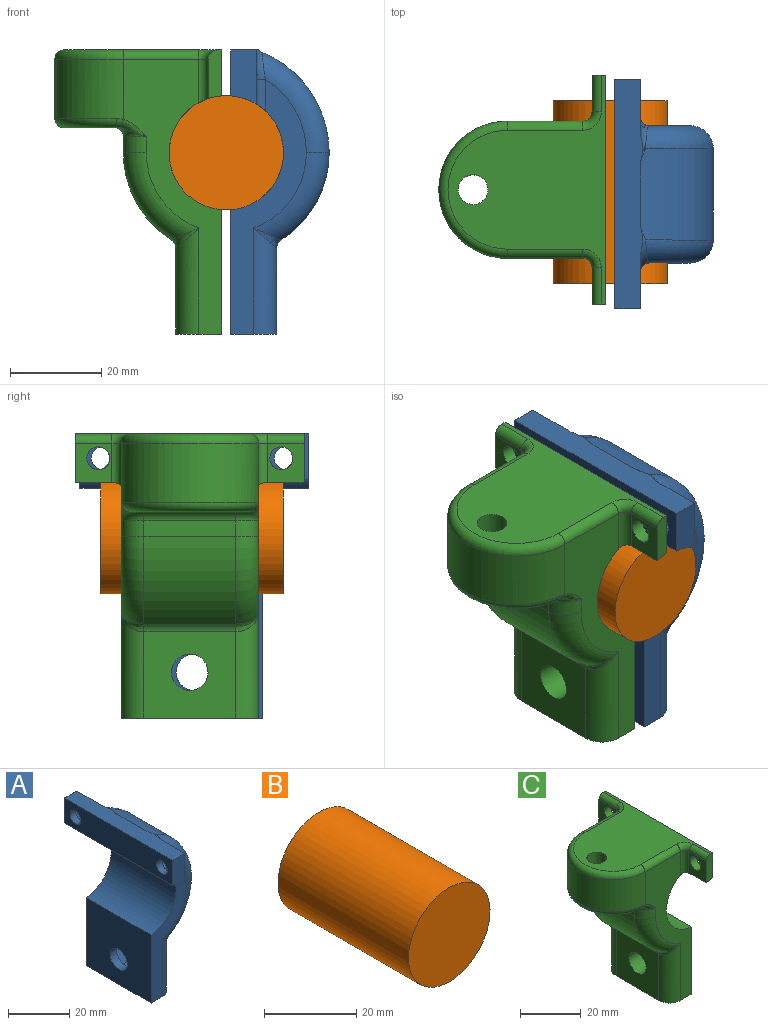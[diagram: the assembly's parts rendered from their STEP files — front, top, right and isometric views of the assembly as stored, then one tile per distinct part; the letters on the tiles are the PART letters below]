
ASSEMBLY  parts=3 mates=2
PART A: 51 faces, bbox 23.8x50.3x63.8 mm
  f0: cylinder r=2.5mm len=5mm, axis (-1,0,0), area 40mm2, adj f8,f37
  f1: cylinder r=2.5mm len=5mm, axis (-1,0,0), area 40mm2, adj f8,f30
  f2: cylinder r=4mm len=8mm, axis (-1,0,0), area 75.4mm2, adj f10,f13
  f3: plane 30x10mm, normal (0,0,-1), area 289.3mm2, adj f4,f10,f11,f12,f39,f42
  f4: plane 20x18.86mm, normal (1,0,0), area 230.9mm2, adj f3,f14,f15,f16,f17,f18,f19,f39
  f5: cylinder r=22.5mm len=20mm, axis (0,1,0), area 455.2mm2, adj f6,f40,f43,f45
  f6: cylinder r=23.81mm len=22.48mm, axis (0,1,0), area 582.6mm2, adj f5,f7,f38,f41,f48,f50
  f7: plane 50.33x6.43mm, normal (0,0,1), area 281.6mm2, adj f6,f8,f20,f21,f22,f23,f48,f50
  f8: plane 50x10.02mm, normal (-1,0,0), area 461.6mm2, adj f0,f1,f7,f9,f20,f23
  f9: cylinder r=12.5mm len=50mm, axis (0,1,0), area 1240.8mm2, adj f8,f10,f11,f12,f20,f21,f22,f23
  f10: plane 30x27.17mm, normal (-1,0,0), area 764.8mm2, adj f2,f3,f9,f11,f12
  f11: plane 55.65x16.5mm, normal (0,-1,0), area 302mm2, adj f3,f9,f10,f41,f42,f43,f47
  f12: plane 55.65x16.5mm, normal (0,1,0), area 302mm2, adj f3,f9,f10,f38,f39,f40,f49
  f13: plane 15.01x13mm, normal (1,0,0), area 96.1mm2, adj f2,f14,f15,f16,f17,f18,f19
  f14: plane 7.51x7mm, normal (0,0,1), area 52.5mm2, adj f4,f13,f15,f19
  f15: plane 7x6.5mm, normal (0,-0.87,0.5), area 52.5mm2, adj f4,f13,f14,f16
  f16: plane 7x6.5mm, normal (0,-0.87,-0.5), area 52.5mm2, adj f4,f13,f15,f17
  f17: plane 7.51x7mm, normal (0,0,-1), area 52.5mm2, adj f4,f13,f16,f18
  f18: plane 7x6.5mm, normal (0,0.87,-0.5), area 52.5mm2, adj f4,f13,f17,f19
  f19: plane 7x6.5mm, normal (0,0.87,0.5), area 52.5mm2, adj f4,f13,f14,f18
  f20: plane 11.83x5.55mm, normal (0,1,0), area 59.2mm2, adj f7,f8,f9,f21
  f21: plane 11.83x10.98mm, normal (1,0,0), area 59.4mm2, adj f7,f9,f20,f24,f25,f26,f27,f28
  f22: plane 11.83x10.98mm, normal (1,0,0), area 59.4mm2, adj f7,f9,f23,f31,f32,f33,f34,f35
  f23: plane 11.83x5.55mm, normal (0,-1,0), area 59.2mm2, adj f7,f8,f9,f22
  f24: plane 3.5x3mm, normal (0,-0.87,0.5), area 12.1mm2, adj f21,f25,f29,f30
  f25: plane 3.5x3mm, normal (0,-0.87,-0.5), area 12.1mm2, adj f21,f24,f26,f30
  f26: plane 4.04x3mm, normal (0,0,-1), area 12.1mm2, adj f21,f25,f27,f30
  f27: plane 3.59x3.33mm, normal (0,0.87,-0.5), area 12.2mm2, adj f21,f26,f28,f30,f50
  f28: plane 3.55x3.3mm, normal (0,0.87,0.5), area 12.3mm2, adj f21,f27,f29,f30,f49,f50
  f29: plane 4.04x3mm, normal (0,0,1), area 12.1mm2, adj f21,f24,f28,f30
  f30: plane 8.08x7mm, normal (1,0,0), area 22.8mm2, adj f1,f24,f25,f26,f27,f28,f29
  f31: plane 4.04x3mm, normal (0,0,1), area 12.1mm2, adj f22,f32,f36,f37
  f32: plane 3.55x3.3mm, normal (0,-0.87,0.5), area 12.3mm2, adj f22,f31,f33,f37,f47,f48
  f33: plane 3.59x3.33mm, normal (0,-0.87,-0.5), area 12.2mm2, adj f22,f32,f34,f37,f48
  f34: plane 4.04x3mm, normal (0,0,-1), area 12.1mm2, adj f22,f33,f35,f37
  f35: plane 3.5x3mm, normal (0,0.87,-0.5), area 12.1mm2, adj f22,f34,f36,f37
  f36: plane 3.5x3mm, normal (0,0.87,0.5), area 12.1mm2, adj f22,f31,f35,f37
  f37: plane 8.08x7mm, normal (1,0,0), area 22.8mm2, adj f0,f31,f32,f33,f34,f35,f36
  f38: torus R=18.81mm, axis (0,-1,0), area 190.4mm2, adj f6,f12,f40,f50
  f39: cylinder r=5mm len=23.19mm, axis (0,0,1), area 165.1mm2, adj f3,f4,f12,f44
  f40: torus R=17.5mm, axis (0,-1,0), area 180.6mm2, adj f5,f12,f38,f44
  f41: torus R=18.81mm, axis (0,-1,0), area 190.4mm2, adj f6,f11,f43,f48
  f42: cylinder r=5mm len=23.19mm, axis (0,0,-1), area 165.1mm2, adj f3,f4,f11,f46
  f43: torus R=17.5mm, axis (0,-1,0), area 180.6mm2, adj f5,f11,f41,f46
  f44: bspline ~5.94x5.88mm, area 7mm2, adj f39,f40,f45
  f45: cylinder r=2mm len=20mm, axis (0,1,0), area 40.5mm2, adj f4,f5,f44,f46
  f46: bspline ~5.94x5.88mm, area 7mm2, adj f42,f43,f45
  f47: cylinder r=2mm len=6.9mm, axis (0,0,-1), area 19.1mm2, adj f9,f11,f22,f32,f48
  f48: bspline ~11.63x9.03mm, area 21.2mm2, adj f6,f7,f22,f32,f33,f41,f47
  f49: cylinder r=2mm len=6.9mm, axis (0,0,1), area 19.1mm2, adj f9,f12,f21,f28,f50
  f50: bspline ~11.63x9.03mm, area 21.2mm2, adj f6,f7,f21,f27,f28,f38,f49
PART B: 3 faces, bbox 25x40x25 mm
  f0: cylinder r=12.5mm len=40mm, axis (0,1,0), area 3141.6mm2, adj f1,f2
  f1: plane 25x25mm, normal (0,-1,0), area 490.9mm2, adj f0
  f2: plane 25x25mm, normal (0,1,0), area 490.9mm2, adj f0
PART C: 46 faces, bbox 38x50.2x62.3 mm
  f0: plane 60.11x21.5mm, normal (0,-1,0), area 483.7mm2, adj f6,f7,f8,f11,f23,f24,f25,f27
  f1: plane 50x10.02mm, normal (1,0,0), area 461.6mm2, adj f2,f8,f15,f17,f18,f19
  f2: plane 50x34.5mm, normal (0,0,1), area 822.1mm2, adj f1,f10,f15,f17,f26,f28,f29,f30
  f3: plane 20x3.48mm, normal (-1,0,0), area 69.6mm2, adj f4,f22,f25,f42
  f4: cylinder r=22.5mm len=20mm, axis (0,1,0), area 455.2mm2, adj f3,f21,f24,f36
  f5: plane 20x18.86mm, normal (-1,0,0), area 327mm2, adj f6,f13,f20,f23,f36
  f6: plane 30x10mm, normal (0,0,-1), area 289.3mm2, adj f0,f5,f7,f9,f20,f23
  f7: plane 30x27.17mm, normal (1,0,0), area 764.8mm2, adj f0,f6,f8,f9,f13
  f8: cylinder r=12.5mm len=50mm, axis (0,1,0), area 1181.3mm2, adj f0,f1,f7,f9,f14,f15,f16,f17
  f9: plane 60.34x21.74mm, normal (0,1,0), area 483.7mm2, adj f6,f7,f8,f11,f20,f21,f22,f31
  f10: cylinder r=3.25mm len=17mm, axis (0,0,1), area 347.1mm2, adj f2,f12
  f11: cylinder r=15mm len=30mm, axis (0,0,1), area 612.9mm2, adj f0,f9,f30,f39,f41,f43
  f12: plane 25.86x11.64mm, normal (0,0,-1), area 181.7mm2, adj f10,f40,f41,f42,f45
  f13: cylinder r=4mm len=10mm, axis (-1,0,0), area 251.3mm2, adj f5,f7
  f14: plane 8.64x8mm, normal (-1,0,0), area 49.4mm2, adj f8,f15,f19,f26,f27
  f15: plane 10.64x3mm, normal (0,-1,0), area 29.9mm2, adj f1,f2,f8,f14,f26
  f16: plane 8.64x8mm, normal (-1,0,0), area 49.4mm2, adj f8,f17,f18,f32,f34
  f17: plane 10.64x3mm, normal (0,1,0), area 29.9mm2, adj f1,f2,f8,f16,f34
  f18: cylinder r=2.5mm len=5mm, axis (-1,0,0), area 47.1mm2, adj f1,f16
  f19: cylinder r=2.5mm len=5mm, axis (-1,0,0), area 47.1mm2, adj f1,f14
  f20: cylinder r=5mm len=23.19mm, axis (0,0,-1), area 160mm2, adj f5,f6,f9,f35
  f21: torus R=17.5mm, axis (0,-1,0), area 174.6mm2, adj f4,f9,f22,f35
  f22: cylinder r=5mm len=5mm, axis (0,0,-1), area 27.3mm2, adj f3,f9,f21,f40
  f23: cylinder r=5mm len=23.19mm, axis (0,0,1), area 160mm2, adj f0,f5,f6,f37
  f24: torus R=17.5mm, axis (0,-1,0), area 174.6mm2, adj f0,f4,f25,f37
  f25: cylinder r=5mm len=5mm, axis (0,0,1), area 27.3mm2, adj f0,f3,f24,f45
  f26: cylinder r=2mm len=8mm, axis (0,-1,0), area 25.1mm2, adj f2,f14,f15,f28
  f27: cylinder r=2mm len=9.51mm, axis (0,0,-1), area 28mm2, adj f0,f8,f14,f28
  f28: torus R=4mm, axis (0,0,1), area 13.5mm2, adj f2,f26,f27,f29
  f29: cylinder r=2mm len=16.5mm, axis (1,0,0), area 51.8mm2, adj f0,f2,f28,f30
  f30: torus R=13mm, axis (0,0,1), area 140.9mm2, adj f2,f11,f29,f31
  f31: cylinder r=2mm len=16.5mm, axis (-1,0,0), area 51.8mm2, adj f2,f9,f30,f33
  f32: cylinder r=2mm len=9.51mm, axis (0,0,-1), area 28mm2, adj f8,f9,f16,f33
  f33: torus R=4mm, axis (0,0,1), area 13.5mm2, adj f2,f31,f32,f34
  f34: cylinder r=2mm len=8mm, axis (0,-1,0), area 25.1mm2, adj f2,f16,f17,f33
  f35: bspline ~5.94x5.88mm, area 11.1mm2, adj f20,f21,f36
  f36: cylinder r=2mm len=20mm, axis (0,1,0), area 40.5mm2, adj f4,f5,f35,f37
  f37: bspline ~5.94x5.88mm, area 11.1mm2, adj f23,f24,f36
  f38: bspline ~5.97x3.97mm, area 8.8mm2, adj f9,f39,f40
  f39: bspline ~4.01x2.44mm, area 3.6mm2, adj f11,f38,f40,f41
  f40: torus R=7mm, axis (0,0,1), area 15.1mm2, adj f12,f22,f38,f39,f42
  f41: torus R=13mm, axis (0,0,1), area 131.5mm2, adj f11,f12,f39,f43
  f42: cylinder r=2mm len=20mm, axis (0,-1,0), area 62.8mm2, adj f3,f12,f40,f45
  f43: bspline ~4.01x2.44mm, area 3.6mm2, adj f11,f41,f44,f45
  f44: bspline ~5.5x3.83mm, area 9mm2, adj f0,f43,f45
  f45: torus R=7mm, axis (0,0,1), area 15.1mm2, adj f12,f25,f42,f43,f44
PLACE A t=(-54.98,36.81,-9.83)mm
PLACE B rot(axis=(0,1,0),55deg) t=(-38.9,57.31,-9.83)mm
PLACE C t=(-38.9,37.81,-9.83)mm
MATE cylindrical C.f8 <-> B.f0  axis (0,-1,0) through (-38.9,22.81,-9.83)mm
MATE cylindrical A.f9 <-> B.f0  axis (0,-1,0) through (-38.9,21.81,-9.83)mm
